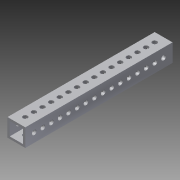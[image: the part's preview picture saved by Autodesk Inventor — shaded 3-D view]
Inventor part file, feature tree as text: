
AUTODESK INVENTOR PART (.ipt)
format: ipt  version: 2013 (Build 170138000, 138)  size: 187,904 bytes
history: native  units: in
note: dims shown in document units (in); Inventor stores cm internally (conversion verified against a paired STEP export)
features: extrude x3, sketch x2
ambient origin geometry x8: Origin, YZ Plane, XZ Plane, XY Plane, X Axis, Y Axis, Z Axis, Center Point
bodies: Solid1 (feature_tree)
feature tree (5):
  extrude  "Extrusion1"  Depth=1.0in
  extrude  "Extrusion2"  Depth=8.25in TaperAngle=0.0deg
  extrude  "Extrusion3"  Depth=0.5in
  sketch  "Sketch1"  dims[d0=1.0in d1=1.0in]
  sketch  "Sketch3"  dims[d2=0.125in d3=8.25in d4=0.0in d5=0.5in d7=0.26in d8=16.5in d9=0.0in d13=8.25in d14=6.2992in d16=0.4833in d17=0.3937in d19=1.0in d21=0.5in d22=8.25in d23=0.26in d24=6.2992in d26=0.4833in d27=0.3937in d29=1.0in d31=1.0in d32=0.0in]
